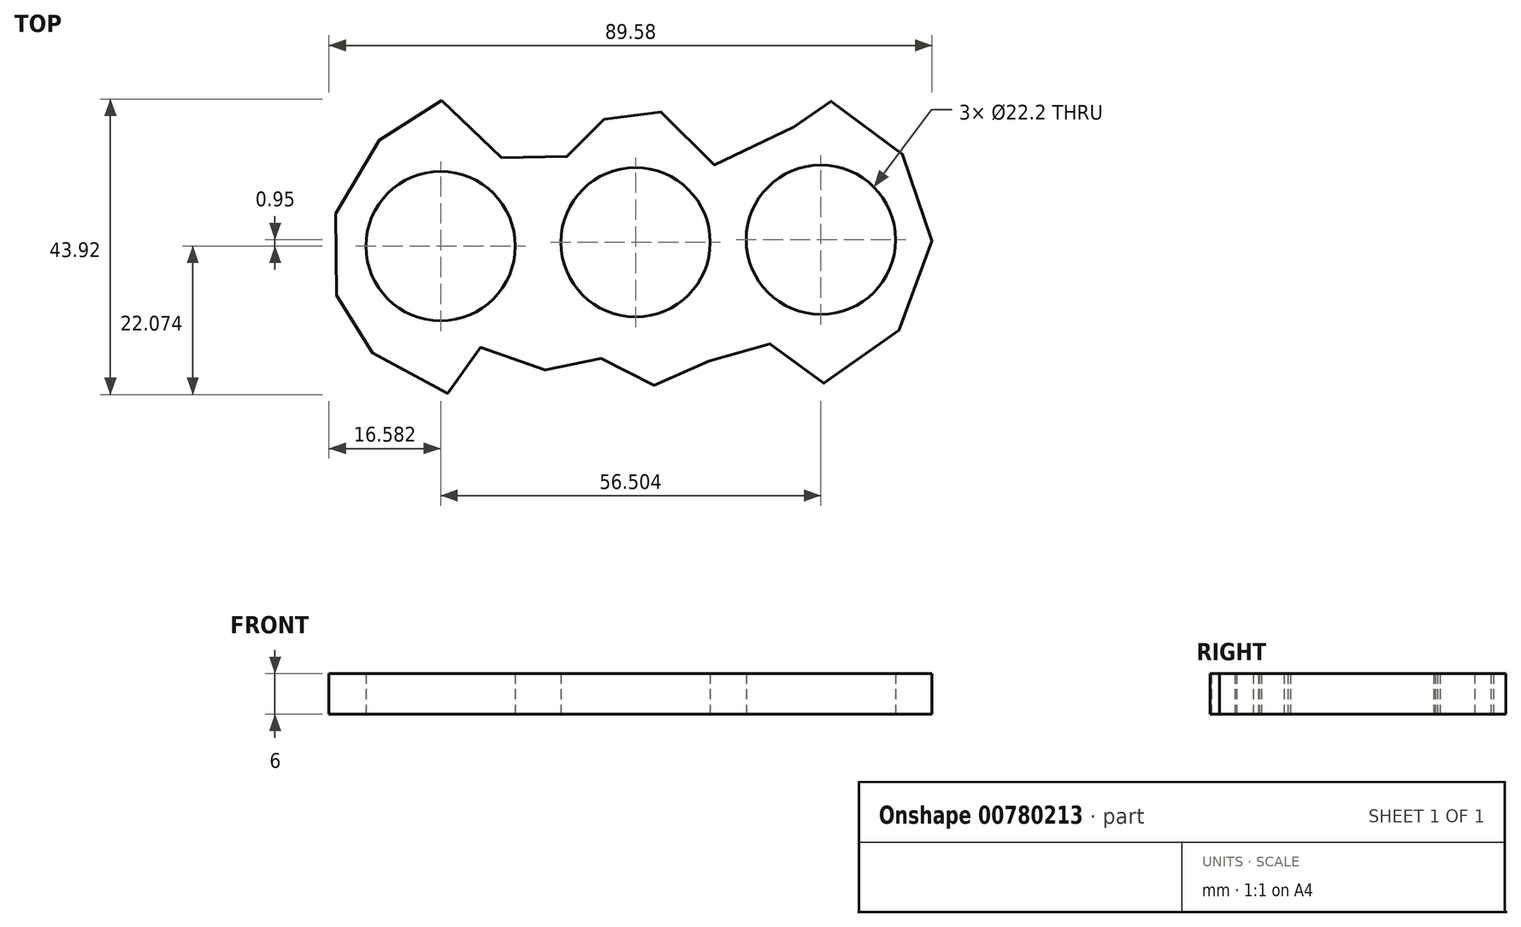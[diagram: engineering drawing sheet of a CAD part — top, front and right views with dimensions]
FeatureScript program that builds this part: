
annotation { "Feature Type Name" : "Feature", "Feature Type Description" : "" }
export const myFeature = defineFeature(function(context is Context, id is Id, definition is map)
    precondition{}
    {
        {
            var Q0;
            Q0=qCreatedBy(makeId("Top.planeOp"),FACE);
            var sketch = newSketch(context, id + "F0", { "sketchPlane" : qUnion([Q0])});
            skPoint(sketch, "E0.13.internal.snap0", {"position": v(35.63, -6.96) * mm});
            skPoint(sketch, "E0.30.internal.snap0", {"position": v(-62.48, -6.96) * mm});
            skFitSpline(sketch, "E0", {"points": [v(-40.94, 14.33) * mm, v(-34.01, 7.58) * mm, v(-26.95, 4.04) * mm, v(-21.46, 7.18) * mm, v(-19.1, 12.29) * mm, v(-12.43, 9.93) * mm, v(-8.5, 12.68) * mm, v(-3.8, 5.61) * mm, v(6.4, 7.18) * mm, v(12.69, 11.9) * mm, v(13.86, 14.25) * mm, v(20.23, 12.88) * mm, v(28.78, 4.44) * mm, v(31.92, -6.96) * mm, v(27.7, -18.9) * mm, v(16.86, -28.06) * mm, v(11.9, -23.43) * mm, v(6.4, -22.25) * mm, v(0, -25.39) * mm, v(-3.4, -22.25) * mm, v(-11.25, -29.31) * mm, v(-16.35, -25.39) * mm, v(-19.1, -23.03) * mm, v(-25.38, -25.78) * mm, v(-30.87, -22.64) * mm, v(-37.15, -23.82) * mm, v(-38.72, -28.92) * mm, v(-48.14, -25.78) * mm, v(-52.85, -21.07) * mm, v(-56.35, -15.05) * mm, v(-57.56, -6.96) * mm, v(-53.22, 5.18) * mm, v(-47.68, 10.48) * mm, v(-40.94, 14.33) * mm]});
            skCircle(sketch, "E1", {"center": v(-41.08, -7.34) * mm, "radius": 11.1 * mm});
            skCircle(sketch, "E2", {"center": v(-12.12, -6.77) * mm, "radius": 11.1 * mm});
            skCircle(sketch, "E3", {"center": v(15.43, -6.39) * mm, "radius": 11.1 * mm});
            skSolve(sketch);
        }
        {
            var Q0;
            Q0=makeQuery(id+"F0.imprint","IMPRINT",FACE,{"disambiguationData":[TD([[makeQuery(id+"F0.imprint","IMPRINT",EDGE,{"derivedFrom":sQuery(id+"F0.wireOp",EDGE,"E0")}),-1.0]])]});
            extrude(context, id + "F1", {"entities" : qUnion([Q0]), "depth" : 6 * mm, "offsetDistance" : 25.4 * mm});
        }
    });
